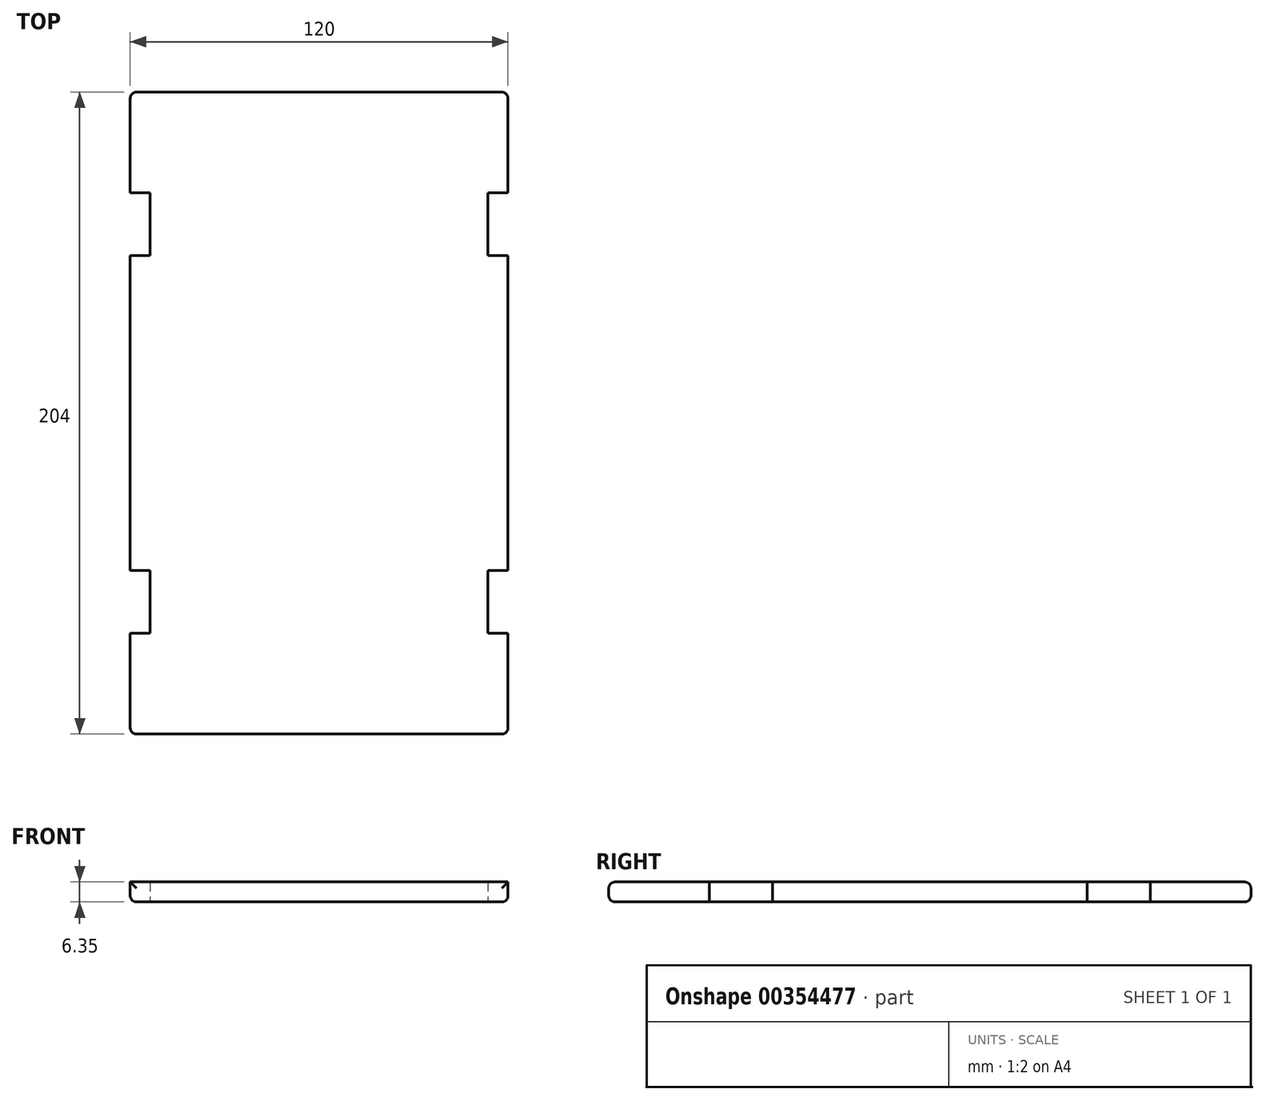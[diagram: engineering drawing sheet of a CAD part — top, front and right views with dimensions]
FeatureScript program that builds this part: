
annotation { "Feature Type Name" : "Feature", "Feature Type Description" : "" }
export const myFeature = defineFeature(function(context is Context, id is Id, definition is map)
    precondition{}
    {
        {
            var Q0;
            Q0=qCreatedBy(makeId("Top.planeOp"),FACE);
            var sketch = newSketch(context, id + "F0", { "sketchPlane" : qUnion([Q0])});
            skLineSegment(sketch, "E0.bottom", {"start": v(-56.81, 134.44) * mm, "end": v(63.19, 134.44) * mm});
            skLineSegment(sketch, "E0.top", {"start": v(-56.81, -69.56) * mm, "end": v(63.19, -69.56) * mm});
            skLineSegment(sketch, "E0.left", {"start": v(-56.81, 134.44) * mm, "end": v(-56.81, -69.56) * mm});
            skLineSegment(sketch, "E0.right", {"start": v(63.19, 134.44) * mm, "end": v(63.19, -69.56) * mm});
            skLineSegment(sketch, "E1.bottom", {"start": v(56.84, 102.44) * mm, "end": v(63.19, 102.44) * mm});
            skLineSegment(sketch, "E1.top", {"start": v(56.84, 82.44) * mm, "end": v(63.19, 82.44) * mm});
            skLineSegment(sketch, "E1.left", {"start": v(56.84, 102.44) * mm, "end": v(56.84, 82.44) * mm});
            skLineSegment(sketch, "E1.right", {"start": v(63.19, 102.44) * mm, "end": v(63.19, 82.44) * mm});
            skLineSegment(sketch, "E2.bottom", {"start": v(-56.81, 82.44) * mm, "end": v(-50.46, 82.44) * mm});
            skLineSegment(sketch, "E2.top", {"start": v(-56.81, 102.44) * mm, "end": v(-50.46, 102.44) * mm});
            skLineSegment(sketch, "E2.left", {"start": v(-56.81, 82.44) * mm, "end": v(-56.81, 102.44) * mm});
            skLineSegment(sketch, "E2.right", {"start": v(-50.46, 82.44) * mm, "end": v(-50.46, 102.44) * mm});
            skLineSegment(sketch, "E3.bottom", {"start": v(-56.81, -37.56) * mm, "end": v(-50.46, -37.56) * mm});
            skLineSegment(sketch, "E3.top", {"start": v(-56.81, -17.56) * mm, "end": v(-50.46, -17.56) * mm});
            skLineSegment(sketch, "E3.left", {"start": v(-56.81, -37.56) * mm, "end": v(-56.81, -17.56) * mm});
            skLineSegment(sketch, "E3.right", {"start": v(-50.46, -37.56) * mm, "end": v(-50.46, -17.56) * mm});
            skLineSegment(sketch, "E4.bottom", {"start": v(56.84, -37.56) * mm, "end": v(63.19, -37.56) * mm});
            skLineSegment(sketch, "E4.top", {"start": v(56.84, -17.56) * mm, "end": v(63.19, -17.56) * mm});
            skLineSegment(sketch, "E4.left", {"start": v(56.84, -37.56) * mm, "end": v(56.84, -17.56) * mm});
            skLineSegment(sketch, "E4.right", {"start": v(63.19, -37.56) * mm, "end": v(63.19, -17.56) * mm});
            skPoint(sketch, "E5.visualSharp", {"position": v(-56.81, -69.56) * mm});
            skPoint(sketch, "E6.visualSharp", {"position": v(63.19, -69.56) * mm});
            skPoint(sketch, "E7.visualSharp", {"position": v(63.19, 134.44) * mm});
            skPoint(sketch, "E8.visualSharp", {"position": v(-56.81, 134.44) * mm});
            skSolve(sketch);
        }
        {
            var Q0;
            Q0=makeQuery(id+"F0.imprint","IMPRINT",FACE,{"disambiguationData":[TD([[makeQuery(id+"F0.imprint","IMPRINT",EDGE,{"derivedFrom":sQuery(id+"F0.wireOp",EDGE,"E0.bottom")}),-1.0]])]});
            extrude(context, id + "F1", {"entities" : qUnion([Q0]), "depth" : 6.35 * mm});
        }
        {
            var Q0;
            Q0=makeQuery(id+"F1.opExtrude","CAP_EDGE",EDGE,{"disambiguationData":[OSD([sQuery(id+"F0.wireOp",EDGE,"E0.top")])],"isStart":false});
            var Q1;
            Q1=makeQuery(id+"F1.opExtrude","CAP_EDGE",EDGE,{"disambiguationData":[OSD([sQuery(id+"F0.wireOp",EDGE,"E0.top")])],"isStart":true});
            var Q2;
            Q2=makeQuery(id+"F1.opExtrude","CAP_EDGE",EDGE,{"disambiguationData":[OSD([sQuery(id+"F0.wireOp",EDGE,"E0.bottom")])],"isStart":false});
            var Q3;
            Q3=makeQuery(id+"F1.opExtrude","CAP_EDGE",EDGE,{"disambiguationData":[OSD([sQuery(id+"F0.wireOp",EDGE,"E0.bottom")])],"isStart":true});
            var Q4;
            Q4=makeQuery(id+"F1.opExtrude","SWEPT_EDGE",EDGE,{"disambiguationData":[OSD([sQuery(id+"F0.wireOp",EDGE,"E0.bottom"),sQuery(id+"F0.wireOp",EDGE,"E0.right")])]});
            var Q5;
            Q5=makeQuery(id+"F1.opExtrude","SWEPT_EDGE",EDGE,{"disambiguationData":[OSD([sQuery(id+"F0.wireOp",EDGE,"E0.bottom"),sQuery(id+"F0.wireOp",EDGE,"E0.left")])]});
            var Q6;
            Q6=makeQuery(id+"F1.opExtrude","SWEPT_EDGE",EDGE,{"disambiguationData":[OSD([sQuery(id+"F0.wireOp",EDGE,"E0.top"),sQuery(id+"F0.wireOp",EDGE,"E0.right")])]});
            var Q7;
            Q7=makeQuery(id+"F1.opExtrude","SWEPT_EDGE",EDGE,{"disambiguationData":[OSD([sQuery(id+"F0.wireOp",EDGE,"E0.top"),sQuery(id+"F0.wireOp",EDGE,"E0.left")])]});
            var Q8;
            {var subQ0=sQuery(id+"F0.wireOp",EDGE,"E0.right");Q8=makeQuery(id+"F1.opExtrude","CAP_EDGE",EDGE,{"disambiguationData":[OSD([subQ0]),TDD([makeQuery(id+"F0.imprint","IMPRINT",EDGE,{"disambiguationData":[TD([[makeQuery(id+"F0.imprint","INTERSECT",VERTEX,{"derivedFrom":[subQ0,sQuery(id+"F0.wireOp",EDGE,"E1.top"),sQuery(id+"F0.wireOp",EDGE,"E1.right")]}),-1.0]])],"derivedFrom":subQ0})])],"isStart":true});}
            var Q9;
            {var subQ0=sQuery(id+"F0.wireOp",EDGE,"E0.right");Q9=makeQuery(id+"F1.opExtrude","CAP_EDGE",EDGE,{"disambiguationData":[OSD([subQ0]),TDD([makeQuery(id+"F0.imprint","IMPRINT",EDGE,{"disambiguationData":[TD([[makeQuery(id+"F0.imprint","INTERSECT",VERTEX,{"derivedFrom":[sQuery(id+"F0.wireOp",EDGE,"E0.bottom"),subQ0]}),-1.0]])],"derivedFrom":subQ0})])],"isStart":true});}
            var Q10;
            {var subQ0=sQuery(id+"F0.wireOp",EDGE,"E0.right");Q10=makeQuery(id+"F1.opExtrude","CAP_EDGE",EDGE,{"disambiguationData":[OSD([subQ0]),TDD([makeQuery(id+"F0.imprint","IMPRINT",EDGE,{"disambiguationData":[TD([[makeQuery(id+"F0.imprint","INTERSECT",VERTEX,{"derivedFrom":[sQuery(id+"F0.wireOp",EDGE,"E0.top"),subQ0]}),1.0]])],"derivedFrom":subQ0})])],"isStart":true});}
            var Q11;
            {var subQ0=sQuery(id+"F0.wireOp",EDGE,"E0.left");Q11=makeQuery(id+"F1.opExtrude","CAP_EDGE",EDGE,{"disambiguationData":[OSD([subQ0]),TDD([makeQuery(id+"F0.imprint","IMPRINT",EDGE,{"disambiguationData":[TD([[makeQuery(id+"F0.imprint","INTERSECT",VERTEX,{"derivedFrom":[sQuery(id+"F0.wireOp",EDGE,"E0.top"),subQ0]}),1.0]])],"derivedFrom":subQ0})])],"isStart":true});}
            var Q12;
            {var subQ0=sQuery(id+"F0.wireOp",EDGE,"E0.left");Q12=makeQuery(id+"F1.opExtrude","CAP_EDGE",EDGE,{"disambiguationData":[OSD([subQ0]),TDD([makeQuery(id+"F0.imprint","IMPRINT",EDGE,{"disambiguationData":[TD([[makeQuery(id+"F0.imprint","INTERSECT",VERTEX,{"derivedFrom":[subQ0,sQuery(id+"F0.wireOp",EDGE,"E2.bottom"),sQuery(id+"F0.wireOp",EDGE,"E2.left")]}),-1.0]])],"derivedFrom":subQ0})])],"isStart":true});}
            var Q13;
            {var subQ0=sQuery(id+"F0.wireOp",EDGE,"E0.left");Q13=makeQuery(id+"F1.opExtrude","CAP_EDGE",EDGE,{"disambiguationData":[OSD([subQ0]),TDD([makeQuery(id+"F0.imprint","IMPRINT",EDGE,{"disambiguationData":[TD([[makeQuery(id+"F0.imprint","INTERSECT",VERTEX,{"derivedFrom":[sQuery(id+"F0.wireOp",EDGE,"E0.bottom"),subQ0]}),-1.0]])],"derivedFrom":subQ0})])],"isStart":true});}
            fillet(context, id + "F2", {"entities" : qUnion([Q0, Q1, Q2, Q3, Q4, Q5, Q6, Q7, Q8, Q9, Q10, Q11, Q12, Q13]), "radius" : 2 * mm, "tangentPropagation" : true, "allowEdgeOverflow" : false});
        }
    });
